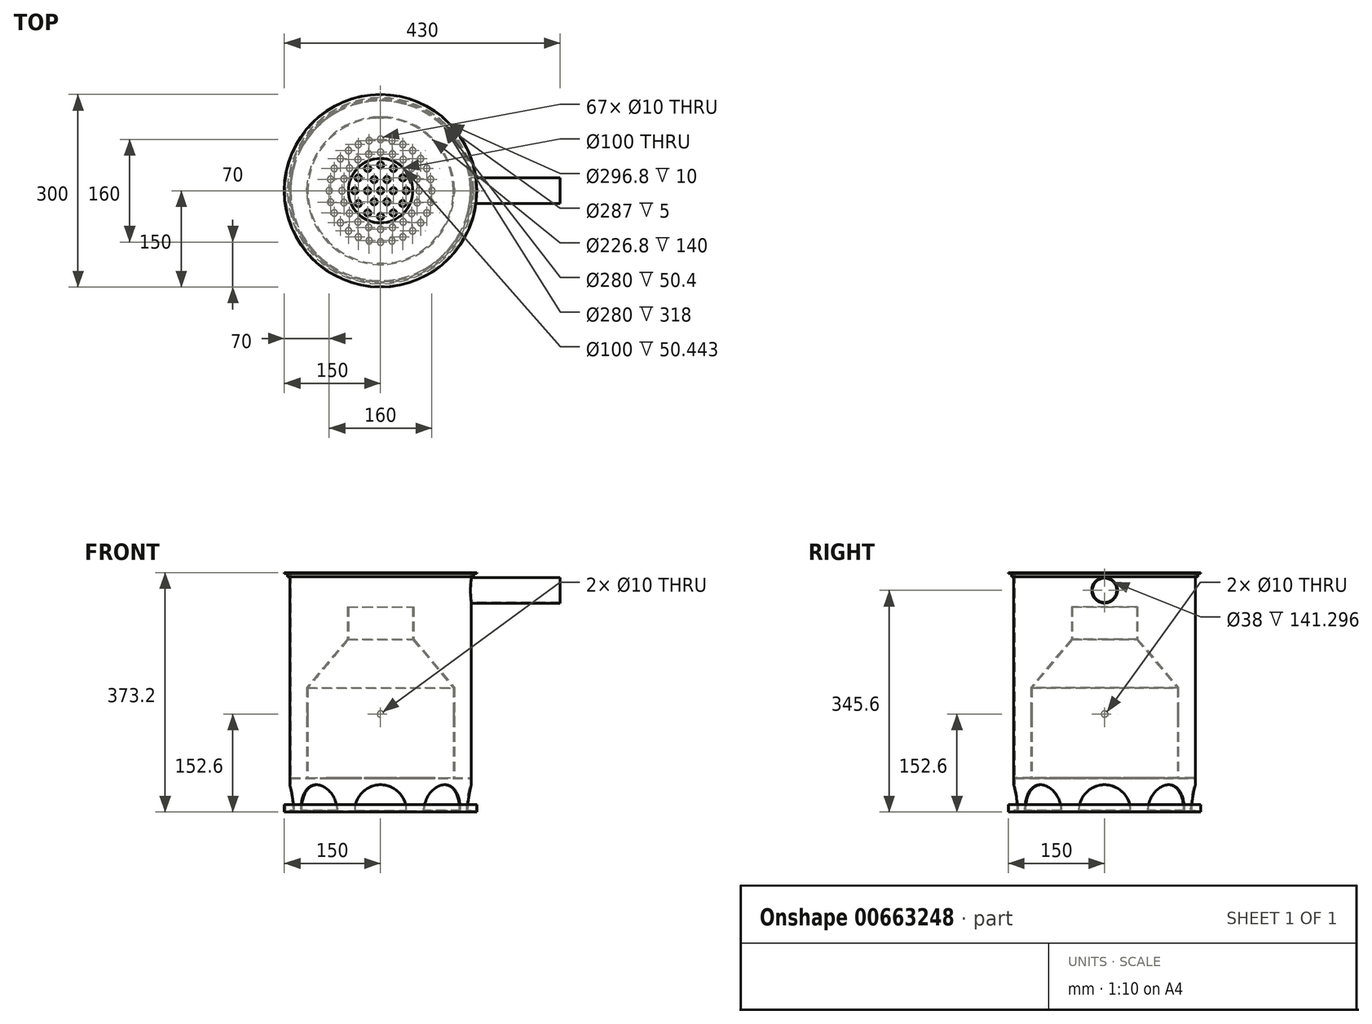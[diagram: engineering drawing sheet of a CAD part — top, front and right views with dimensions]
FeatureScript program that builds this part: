
annotation { "Feature Type Name" : "Feature", "Feature Type Description" : "" }
export const myFeature = defineFeature(function(context is Context, id is Id, definition is map)
    precondition{}
    {
        {
            var Q0;
            Q0=qCreatedBy(makeId("Front.planeOp"),FACE);
            var sketch = newSketch(context, id + "F0", { "sketchPlane" : qUnion([Q0])});
            skLineSegment(sketch, "E0", {"start": v(140, 0) * mm, "end": v(141.6, 0) * mm});
            skLineSegment(sketch, "E1", {"start": v(141.6, 0) * mm, "end": v(141.6, 370) * mm});
            skLineSegment(sketch, "E2.1", {"start": v(140, 0) * mm, "end": v(140, 370) * mm});
            skLineSegment(sketch, "E3", {"start": v(0, 50.4) * mm, "end": v(140, 50.4) * mm});
            skLineSegment(sketch, "E4", {"start": v(0, 50.4) * mm, "end": v(0, 52) * mm});
            skLineSegment(sketch, "E5", {"start": v(0, 52) * mm, "end": v(140, 52) * mm});
            skLineSegment(sketch, "E6", {"start": v(50, 318) * mm, "end": v(51.6, 318) * mm});
            skLineSegment(sketch, "E7", {"start": v(50, 318) * mm, "end": v(50, 267.56) * mm});
            skLineSegment(sketch, "E8", {"start": v(50, 267.56) * mm, "end": v(113.4, 192) * mm});
            skLineSegment(sketch, "E9", {"start": v(113.4, 192) * mm, "end": v(113.4, 52) * mm});
            skLineSegment(sketch, "E10.0", {"start": v(115, 192.58) * mm, "end": v(115, 52) * mm});
            skLineSegment(sketch, "E10.1", {"start": v(51.6, 268.14) * mm, "end": v(115, 192.58) * mm});
            skLineSegment(sketch, "E10.2", {"start": v(51.6, 318) * mm, "end": v(51.6, 268.14) * mm});
            skLineSegment(sketch, "E11", {"start": v(0, 1) * mm, "end": v(0, 370) * mm, "construction": true});
            skPoint(sketch, "E12.end.orphan", {"position": v(50, 369) * mm});
            skPoint(sketch, "E12.start.orphan", {"position": v(50, 370) * mm});
            skLineSegment(sketch, "E13", {"start": v(141.6, 370) * mm, "end": v(140, 370) * mm});
            skPoint(sketch, "E14.start.orphan", {"position": v(50, 319) * mm});
            skPoint(sketch, "E15.end.orphan", {"position": v(0, 0) * mm});
            skSolve(sketch);
        }
        {
            var Q0;
            Q0=makeQuery(id+"F0.imprint","IMPRINT",FACE,{"disambiguationData":[TD([[makeQuery(id+"F0.imprint","IMPRINT",EDGE,{"derivedFrom":sQuery(id+"F0.wireOp",EDGE,"E0")}),1.0]])]});
            var Q1;
            {var subQ3=sQuery(id+"F0.wireOp",EDGE,"E3");Q1=makeQuery(id+"F0.imprint","IMPRINT",FACE,{"disambiguationData":[TD([[makeQuery(id+"F0.imprint","IMPRINT",EDGE,{"derivedFrom":subQ3}),1.0]])]});}
            var Q2;
            {var subQ0=sQuery(id+"F0.wireOp",EDGE,"E7");Q2=makeQuery(id+"F0.imprint","IMPRINT",FACE,{"disambiguationData":[TD([[makeQuery(id+"F0.imprint","IMPRINT",EDGE,{"derivedFrom":subQ0}),1.0]])]});}
            var Q3;
            {var subQ3=sQuery(id+"F0.wireOp",EDGE,"OUD1FrWK-T3TI-8EPN-yAmI-f2VSRblGpb5R");Q3=makeQuery(id+"F0.imprint","IMPRINT",FACE,{"disambiguationData":[TD([[makeQuery(id+"F0.imprint","IMPRINT",EDGE,{"derivedFrom":subQ3}),-1.0]])]});}
            var Q4;
            Q4=sQuery(id+"F0.wireOp",EDGE,"E11");
            revolve(context, id + "F1", {"entities" : qUnion([Q0, Q1, Q2, Q3]), "axis" : qUnion([Q4]), "revolveType" : RevolveType.FULL});
        }
        {
            var Q0;
            {var subQ0=sQuery(id+"F0.wireOp",EDGE,"E5");Q0=makeQuery(id+"F1.opRevolve","SWEPT_FACE",FACE,{"disambiguationData":[OSD([subQ0]),TDD([makeQuery(id+"F0.imprint","IMPRINT",EDGE,{"disambiguationData":[TD([[makeQuery(id+"F0.imprint","INTERSECT",VERTEX,{"derivedFrom":[sQuery(id+"F0.wireOp",EDGE,"E4"),subQ0]}),-1.0]])],"derivedFrom":subQ0})])]});}
            var sketch = newSketch(context, id + "F2", { "sketchPlane" : qUnion([Q0])});
            skCircle(sketch, "E16", {"center": v(0, 0) * mm, "radius": 5 * mm});
            skCircle(sketch, "E17", {"center": v(20, 0) * mm, "radius": 5 * mm});
            skCircle(sketch, "E18.1.0", {"center": v(10, 17.32) * mm, "radius": 5 * mm});
            skCircle(sketch, "E18.2.0", {"center": v(-10, 17.32) * mm, "radius": 5 * mm});
            skCircle(sketch, "E19.1.3.0", {"center": v(-20, 0) * mm, "radius": 5 * mm});
            skCircle(sketch, "E20", {"center": v(40, 0) * mm, "radius": 5 * mm});
            skCircle(sketch, "E21.1.0", {"center": v(34.64, 20) * mm, "radius": 5 * mm});
            skCircle(sketch, "E21.2.0", {"center": v(20, 34.64) * mm, "radius": 5 * mm});
            skCircle(sketch, "E22.1.3.0", {"center": v(0, 40) * mm, "radius": 5 * mm});
            skCircle(sketch, "E22.1.4.0", {"center": v(-20, 34.64) * mm, "radius": 5 * mm});
            skCircle(sketch, "E22.1.5.0", {"center": v(-34.64, 20) * mm, "radius": 5 * mm});
            skCircle(sketch, "E22.1.6.0", {"center": v(-40, 0) * mm, "radius": 5 * mm});
            skCircle(sketch, "E22.1.7.0", {"center": v(-34.64, -20) * mm, "radius": 5 * mm});
            skCircle(sketch, "E23", {"center": v(60, 0) * mm, "radius": 5 * mm});
            skCircle(sketch, "E24", {"center": v(80, 0) * mm, "radius": 5 * mm});
            skCircle(sketch, "E25.1.0", {"center": v(57.06, 18.54) * mm, "radius": 5 * mm});
            skCircle(sketch, "E25.2.0", {"center": v(48.54, 35.27) * mm, "radius": 5 * mm});
            skCircle(sketch, "E26.1.3.0", {"center": v(35.27, 48.54) * mm, "radius": 5 * mm});
            skCircle(sketch, "E26.1.4.0", {"center": v(18.54, 57.06) * mm, "radius": 5 * mm});
            skCircle(sketch, "E26.1.5.0", {"center": v(0, 60) * mm, "radius": 5 * mm});
            skCircle(sketch, "E26.1.6.0", {"center": v(-18.54, 57.06) * mm, "radius": 5 * mm});
            skCircle(sketch, "E26.1.7.0", {"center": v(-35.27, 48.54) * mm, "radius": 5 * mm});
            skCircle(sketch, "E26.1.8.0", {"center": v(-48.54, 35.27) * mm, "radius": 5 * mm});
            skCircle(sketch, "E26.1.9.0", {"center": v(-57.06, 18.54) * mm, "radius": 5 * mm});
            skCircle(sketch, "E26.1.10.0", {"center": v(-60, 0) * mm, "radius": 5 * mm});
            skCircle(sketch, "E26.1.11.0", {"center": v(-57.06, -18.54) * mm, "radius": 5 * mm});
            skCircle(sketch, "E26.1.12.0", {"center": v(-48.54, -35.27) * mm, "radius": 5 * mm});
            skCircle(sketch, "E26.1.13.0", {"center": v(-35.27, -48.54) * mm, "radius": 5 * mm});
            skCircle(sketch, "E26.1.14.0", {"center": v(-18.54, -57.06) * mm, "radius": 5 * mm});
            skCircle(sketch, "E26.1.15.0", {"center": v(0, -60) * mm, "radius": 5 * mm});
            skCircle(sketch, "E26.1.16.0", {"center": v(18.54, -57.06) * mm, "radius": 5 * mm});
            skCircle(sketch, "E26.1.17.0", {"center": v(35.27, -48.54) * mm, "radius": 5 * mm});
            skCircle(sketch, "E26.1.18.0", {"center": v(48.54, -35.27) * mm, "radius": 5 * mm});
            skCircle(sketch, "E26.1.19.0", {"center": v(57.06, -18.54) * mm, "radius": 5 * mm});
            skCircle(sketch, "E27.1.8.0", {"center": v(-20, -34.64) * mm, "radius": 5 * mm});
            skCircle(sketch, "E27.1.9.0", {"center": v(0, -40) * mm, "radius": 5 * mm});
            skCircle(sketch, "E27.1.10.0", {"center": v(20, -34.64) * mm, "radius": 5 * mm});
            skCircle(sketch, "E27.1.11.0", {"center": v(34.64, -20) * mm, "radius": 5 * mm});
            skCircle(sketch, "E28.1.0", {"center": v(78, 17.8) * mm, "radius": 5 * mm});
            skCircle(sketch, "E28.2.0", {"center": v(72.08, 34.71) * mm, "radius": 5 * mm});
            skCircle(sketch, "E29.1.3.0", {"center": v(62.55, 49.88) * mm, "radius": 5 * mm});
            skCircle(sketch, "E29.1.4.0", {"center": v(49.88, 62.55) * mm, "radius": 5 * mm});
            skCircle(sketch, "E29.1.5.0", {"center": v(34.71, 72.08) * mm, "radius": 5 * mm});
            skCircle(sketch, "E29.1.6.0", {"center": v(17.8, 78) * mm, "radius": 5 * mm});
            skCircle(sketch, "E29.1.7.0", {"center": v(0, 80) * mm, "radius": 5 * mm});
            skCircle(sketch, "E29.1.8.0", {"center": v(-17.8, 78) * mm, "radius": 5 * mm});
            skCircle(sketch, "E29.1.9.0", {"center": v(-34.71, 72.08) * mm, "radius": 5 * mm});
            skCircle(sketch, "E29.1.10.0", {"center": v(-49.88, 62.55) * mm, "radius": 5 * mm});
            skCircle(sketch, "E29.1.11.0", {"center": v(-62.55, 49.88) * mm, "radius": 5 * mm});
            skCircle(sketch, "E29.1.12.0", {"center": v(-72.08, 34.71) * mm, "radius": 5 * mm});
            skCircle(sketch, "E29.1.13.0", {"center": v(-78, 17.8) * mm, "radius": 5 * mm});
            skCircle(sketch, "E29.1.14.0", {"center": v(-80, 0) * mm, "radius": 5 * mm});
            skCircle(sketch, "E29.1.15.0", {"center": v(-78, -17.8) * mm, "radius": 5 * mm});
            skCircle(sketch, "E29.1.16.0", {"center": v(-72.08, -34.71) * mm, "radius": 5 * mm});
            skCircle(sketch, "E29.1.17.0", {"center": v(-62.55, -49.88) * mm, "radius": 5 * mm});
            skCircle(sketch, "E29.1.18.0", {"center": v(-49.88, -62.55) * mm, "radius": 5 * mm});
            skCircle(sketch, "E29.1.19.0", {"center": v(-34.71, -72.08) * mm, "radius": 5 * mm});
            skCircle(sketch, "E29.1.20.0", {"center": v(-17.8, -78) * mm, "radius": 5 * mm});
            skCircle(sketch, "E29.1.21.0", {"center": v(0, -80) * mm, "radius": 5 * mm});
            skCircle(sketch, "E29.1.22.0", {"center": v(17.8, -78) * mm, "radius": 5 * mm});
            skCircle(sketch, "E29.1.23.0", {"center": v(34.71, -72.08) * mm, "radius": 5 * mm});
            skCircle(sketch, "E29.1.24.0", {"center": v(49.88, -62.55) * mm, "radius": 5 * mm});
            skCircle(sketch, "E29.1.25.0", {"center": v(62.55, -49.88) * mm, "radius": 5 * mm});
            skCircle(sketch, "E29.1.26.0", {"center": v(72.08, -34.71) * mm, "radius": 5 * mm});
            skCircle(sketch, "E29.1.27.0", {"center": v(78, -17.8) * mm, "radius": 5 * mm});
            skCircle(sketch, "E30.1.4.0", {"center": v(-10, -17.32) * mm, "radius": 5 * mm});
            skCircle(sketch, "E30.1.5.0", {"center": v(10, -17.32) * mm, "radius": 5 * mm});
            skSolve(sketch);
        }
        {
            var Q0;
            Q0=qSketchRegion(id+"F2",true);
            var Q1;
            Q1=makeQuery(id+"F1.opRevolve","SWEPT_FACE",FACE,{"disambiguationData":[OSD([sQuery(id+"F0.wireOp",EDGE,"E3")])]});
            extrude(context, id + "F3", {"entities" : qUnion([Q0]), "operationType" : NewBodyOperationType.REMOVE, "endBound" : BoundingType.UP_TO_SURFACE, "oppositeDirection" : true, "depth" : 1 * mm, "endBoundEntityFace" : qUnion([Q1]), "offsetDistance" : 25 * mm});
        }
        {
            var Q0;
            Q0=qCreatedBy(makeId("Right.planeOp"),FACE);
            var sketch = newSketch(context, id + "F4", { "sketchPlane" : qUnion([Q0])});
            skCircle(sketch, "E31", {"center": v(0, 344) * mm, "radius": 20 * mm});
            skSolve(sketch);
        }
        {
            var Q0;
            Q0=makeQuery(id+"F4.imprint","IMPRINT",FACE,{"disambiguationData":[TD([[makeQuery(id+"F4.imprint","IMPRINT",EDGE,{"derivedFrom":sQuery(id+"F4.wireOp",EDGE,"E31")}),1.0]])]});
            var Q1;
            Q1=sQuery(id+"F4.wireOp",EDGE,"E31");
            extrude(context, id + "F5", {"entities" : qUnion([Q0]), "operationType" : NewBodyOperationType.ADD, "surfaceEntities" : qUnion([Q1]), "depth" : 280 * mm, "offsetDistance" : 25 * mm});
        }
        {
            var Q0;
            Q0=makeQuery(id+"F5.opExtrude","CAP_FACE",FACE,{"disambiguationData":[OSD([sQuery(id+"F4.wireOp",EDGE,"E31")])],"isStart":true});
            var sketch = newSketch(context, id + "F6", { "sketchPlane" : qUnion([Q0])});
            skCircle(sketch, "E32", {"center": v(0, 344) * mm, "radius": 19 * mm});
            skSolve(sketch);
        }
        {
            var Q0;
            Q0=makeQuery(id+"F6.imprint","IMPRINT",FACE,{"disambiguationData":[TD([[makeQuery(id+"F6.imprint","IMPRINT",EDGE,{"derivedFrom":sQuery(id+"F6.wireOp",EDGE,"E32")}),1.0]])]});
            extrude(context, id + "F7", {"entities" : qUnion([Q0]), "operationType" : NewBodyOperationType.REMOVE, "endBound" : BoundingType.THROUGH_ALL, "oppositeDirection" : true, "depth" : 25 * mm, "offsetDistance" : 25 * mm});
        }
        {
            var Q0;
            Q0=qCreatedBy(makeId("Front.planeOp"),FACE);
            var sketch = newSketch(context, id + "F8", { "sketchPlane" : qUnion([Q0])});
            skLineSegment(sketch, "E33", {"start": v(0, 1) * mm, "end": v(40, 1) * mm});
            skArc(sketch, "E34", {"start": v(40, 1) * mm, "mid": v(0, 41) * mm, "end": v(-40, 1) * mm});
            skLineSegment(sketch, "E35", {"start": v(0, 1) * mm, "end": v(-40, 1) * mm});
            skSolve(sketch);
        }
        {
            var Q0;
            Q0 = qSketchRegion(id + "F8", true);
            extrude(context, id + "F9", {"entities" : qUnion([Q0]), "depth" : 150 * mm, "offsetDistance" : 25 * mm});
        }
        {
            var Q0;
            Q0=makeQuery(id+"F9.opExtrude","SWEPT_BODY",BODY,{"disambiguationData":[OSD([sQuery(id+"F8.wireOp",EDGE,"E33"),sQuery(id+"F8.wireOp",EDGE,"E34"),sQuery(id+"F8.wireOp",EDGE,"E35")])]});
            var Q1;
            Q1=sQuery(id+"F0.wireOp",EDGE,"E11");
            circularPattern(context, id + "F10", {"entities" : qUnion([Q0]), "axis" : qUnion([Q1]), "angle" : 360 * degree, "instanceCount" : 8, "equalSpace" : true});
        }
        {
            var Q0;
            Q0=makeQuery(id+"F9.opExtrude","SWEPT_BODY",BODY,{"disambiguationData":[OSD([sQuery(id+"F8.wireOp",EDGE,"E33"),sQuery(id+"F8.wireOp",EDGE,"E34"),sQuery(id+"F8.wireOp",EDGE,"E35")])]});
            var Q1;
            Q1=makeQuery(id+"F10.opPattern","COPY",BODY,{"derivedFrom":makeQuery(id+"F9.opExtrude","SWEPT_BODY",BODY,{"disambiguationData":[OSD([sQuery(id+"F8.wireOp",EDGE,"E33"),sQuery(id+"F8.wireOp",EDGE,"E34"),sQuery(id+"F8.wireOp",EDGE,"E35")])]}),"instanceName":"1"});
            var Q2;
            Q2=makeQuery(id+"F10.opPattern","COPY",BODY,{"derivedFrom":makeQuery(id+"F9.opExtrude","SWEPT_BODY",BODY,{"disambiguationData":[OSD([sQuery(id+"F8.wireOp",EDGE,"E33"),sQuery(id+"F8.wireOp",EDGE,"E34"),sQuery(id+"F8.wireOp",EDGE,"E35")])]}),"instanceName":"2"});
            var Q3;
            Q3=makeQuery(id+"F10.opPattern","COPY",BODY,{"derivedFrom":makeQuery(id+"F9.opExtrude","SWEPT_BODY",BODY,{"disambiguationData":[OSD([sQuery(id+"F8.wireOp",EDGE,"E33"),sQuery(id+"F8.wireOp",EDGE,"E34"),sQuery(id+"F8.wireOp",EDGE,"E35")])]}),"instanceName":"3"});
            var Q4;
            Q4=makeQuery(id+"F10.opPattern","COPY",BODY,{"derivedFrom":makeQuery(id+"F9.opExtrude","SWEPT_BODY",BODY,{"disambiguationData":[OSD([sQuery(id+"F8.wireOp",EDGE,"E33"),sQuery(id+"F8.wireOp",EDGE,"E34"),sQuery(id+"F8.wireOp",EDGE,"E35")])]}),"instanceName":"4"});
            var Q5;
            Q5=makeQuery(id+"F10.opPattern","COPY",BODY,{"derivedFrom":makeQuery(id+"F9.opExtrude","SWEPT_BODY",BODY,{"disambiguationData":[OSD([sQuery(id+"F8.wireOp",EDGE,"E33"),sQuery(id+"F8.wireOp",EDGE,"E34"),sQuery(id+"F8.wireOp",EDGE,"E35")])]}),"instanceName":"5"});
            var Q6;
            Q6=makeQuery(id+"F10.opPattern","COPY",BODY,{"derivedFrom":makeQuery(id+"F9.opExtrude","SWEPT_BODY",BODY,{"disambiguationData":[OSD([sQuery(id+"F8.wireOp",EDGE,"E33"),sQuery(id+"F8.wireOp",EDGE,"E34"),sQuery(id+"F8.wireOp",EDGE,"E35")])]}),"instanceName":"6"});
            var Q7;
            Q7=makeQuery(id+"F10.opPattern","COPY",BODY,{"derivedFrom":makeQuery(id+"F9.opExtrude","SWEPT_BODY",BODY,{"disambiguationData":[OSD([sQuery(id+"F8.wireOp",EDGE,"E33"),sQuery(id+"F8.wireOp",EDGE,"E34"),sQuery(id+"F8.wireOp",EDGE,"E35")])]}),"instanceName":"7"});
            var Q8;
            Q8=makeQuery(id+"F1.opRevolve","SWEPT_BODY",BODY,{"disambiguationData":[OSD([sQuery(id+"F0.wireOp",EDGE,"E0"),sQuery(id+"F0.wireOp",EDGE,"E1"),sQuery(id+"F0.wireOp",EDGE,"noxKHUUk-OG0o-8wTU-6CPF-3SisgwZ0xtMZ"),sQuery(id+"F0.wireOp",EDGE,"E2.0"),sQuery(id+"F0.wireOp",EDGE,"E2.1"),sQuery(id+"F0.wireOp",EDGE,"E2.2"),sQuery(id+"F0.wireOp",EDGE,"E12"),sQuery(id+"F0.wireOp",EDGE,"E15"),sQuery(id+"F0.wireOp",EDGE,"E3"),sQuery(id+"F0.wireOp",EDGE,"E4"),sQuery(id+"F0.wireOp",EDGE,"E5"),sQuery(id+"F0.wireOp",EDGE,"OUD1FrWK-T3TI-8EPN-yAmI-f2VSRblGpb5R"),sQuery(id+"F0.wireOp",EDGE,"E14"),sQuery(id+"F0.wireOp",EDGE,"E6"),sQuery(id+"F0.wireOp",EDGE,"E7"),sQuery(id+"F0.wireOp",EDGE,"E8"),sQuery(id+"F0.wireOp",EDGE,"E9"),sQuery(id+"F0.wireOp",EDGE,"E10.0"),sQuery(id+"F0.wireOp",EDGE,"E10.1"),sQuery(id+"F0.wireOp",EDGE,"E10.2")])]});
            booleanBodies(context, id + "F11", {"operationType" : BooleanOperationType.SUBTRACTION, "tools" : qUnion([Q0, Q1, Q2, Q3, Q4, Q5, Q6, Q7]), "targets" : qUnion([Q8])});
        }
        {
            var Q0;
            Q0=qCreatedBy(makeId("Front.planeOp"),FACE);
            var sketch = newSketch(context, id + "F12", { "sketchPlane" : qUnion([Q0])});
            skCircle(sketch, "E36", {"center": v(0, 151) * mm, "radius": 5 * mm});
            skSolve(sketch);
        }
        {
            var Q0;
            Q0 = qSketchRegion(id + "F12", true);
            extrude(context, id + "F13", {"entities" : qUnion([Q0]), "depth" : 128 * mm, "offsetDistance" : 25 * mm});
        }
        {
            var Q0;
            Q0=makeQuery(id+"F13.opExtrude","SWEPT_BODY",BODY,{"disambiguationData":[OSD([sQuery(id+"F12.wireOp",EDGE,"E36")])]});
            var Q1;
            Q1=sQuery(id+"F0.wireOp",EDGE,"E11");
            circularPattern(context, id + "F14", {"entities" : qUnion([Q0]), "axis" : qUnion([Q1]), "angle" : 360 * degree, "instanceCount" : 4, "equalSpace" : true});
        }
        {
            var Q0;
            Q0=makeQuery(id+"F14.opPattern","COPY",BODY,{"derivedFrom":makeQuery(id+"F13.opExtrude","SWEPT_BODY",BODY,{"disambiguationData":[OSD([sQuery(id+"F12.wireOp",EDGE,"E36")])]}),"instanceName":"2"});
            var Q1;
            Q1=makeQuery(id+"F14.opPattern","COPY",BODY,{"derivedFrom":makeQuery(id+"F13.opExtrude","SWEPT_BODY",BODY,{"disambiguationData":[OSD([sQuery(id+"F12.wireOp",EDGE,"E36")])]}),"instanceName":"3"});
            var Q2;
            Q2=makeQuery(id+"F14.opPattern","COPY",BODY,{"derivedFrom":makeQuery(id+"F13.opExtrude","SWEPT_BODY",BODY,{"disambiguationData":[OSD([sQuery(id+"F12.wireOp",EDGE,"E36")])]}),"instanceName":"1"});
            var Q3;
            Q3=makeQuery(id+"F13.opExtrude","SWEPT_BODY",BODY,{"disambiguationData":[OSD([sQuery(id+"F12.wireOp",EDGE,"E36")])]});
            var Q4;
            Q4=makeQuery(id+"F1.opRevolve","SWEPT_BODY",BODY,{"disambiguationData":[OSD([sQuery(id+"F0.wireOp",EDGE,"E0"),sQuery(id+"F0.wireOp",EDGE,"E1"),sQuery(id+"F0.wireOp",EDGE,"noxKHUUk-OG0o-8wTU-6CPF-3SisgwZ0xtMZ"),sQuery(id+"F0.wireOp",EDGE,"E2.0"),sQuery(id+"F0.wireOp",EDGE,"E2.1"),sQuery(id+"F0.wireOp",EDGE,"E2.2"),sQuery(id+"F0.wireOp",EDGE,"E12"),sQuery(id+"F0.wireOp",EDGE,"E15"),sQuery(id+"F0.wireOp",EDGE,"E3"),sQuery(id+"F0.wireOp",EDGE,"E4"),sQuery(id+"F0.wireOp",EDGE,"E5"),sQuery(id+"F0.wireOp",EDGE,"OUD1FrWK-T3TI-8EPN-yAmI-f2VSRblGpb5R"),sQuery(id+"F0.wireOp",EDGE,"E14"),sQuery(id+"F0.wireOp",EDGE,"E6"),sQuery(id+"F0.wireOp",EDGE,"E7"),sQuery(id+"F0.wireOp",EDGE,"E8"),sQuery(id+"F0.wireOp",EDGE,"E9"),sQuery(id+"F0.wireOp",EDGE,"E10.0"),sQuery(id+"F0.wireOp",EDGE,"E10.1"),sQuery(id+"F0.wireOp",EDGE,"E10.2")])]});
            booleanBodies(context, id + "F15", {"operationType" : BooleanOperationType.SUBTRACTION, "tools" : qUnion([Q0, Q1, Q2, Q3]), "targets" : qUnion([Q4])});
        }
        {
            var Q0;
            Q0=makeQuery(id+"F1.opRevolve","SWEPT_FACE",FACE,{"disambiguationData":[OSD([sQuery(id+"F0.wireOp",EDGE,"E13")])]});
            var sketch = newSketch(context, id + "F16", { "sketchPlane" : qUnion([Q0])});
            skCircle(sketch, "E37", {"center": v(0, 0) * mm, "radius": 140 * mm});
            skSolve(sketch);
        }
        {
            var Q0;
            Q0 = qSketchRegion(id + "F16", true);
            var Q1;
            Q1=makeQuery(id+"F1.opRevolve","SWEPT_FACE",FACE,{"disambiguationData":[OSD([sQuery(id+"F0.wireOp",EDGE,"E6")])]});
            extrude(context, id + "F17", {"entities" : qUnion([Q0]), "operationType" : NewBodyOperationType.REMOVE, "endBound" : BoundingType.UP_TO_SURFACE, "oppositeDirection" : true, "depth" : 25 * mm, "endBoundEntityFace" : qUnion([Q1]), "offsetDistance" : 25 * mm});
        }
        {
            var Q0;
            Q0=makeQuery(id+"F1.opRevolve","SWEPT_FACE",FACE,{"disambiguationData":[OSD([sQuery(id+"F0.wireOp",EDGE,"E13")])]});
            var sketch = newSketch(context, id + "F18", { "sketchPlane" : qUnion([Q0])});
            skCircle(sketch, "E38", {"center": v(0, 0) * mm, "radius": 150 * mm});
            skSolve(sketch);
        }
        {
            var Q0;
            Q0 = qSketchRegion(id + "F18", true);
            extrude(context, id + "F19", {"entities" : qUnion([Q0]), "depth" : 1.6 * mm, "offsetDistance" : 25 * mm});
        }
        {
            var Q0;
            Q0=makeQuery(id+"F19.opExtrude","CAP_FACE",FACE,{"disambiguationData":[OSD([sQuery(id+"F18.wireOp",EDGE,"E38")])],"isStart":true});
            var sketch = newSketch(context, id + "F20", { "sketchPlane" : qUnion([Q0])});
            skCircle(sketch, "E39", {"center": v(0, 0) * mm, "radius": 143.5 * mm});
            skCircle(sketch, "E40.0", {"center": v(0, 0) * mm, "radius": 145.1 * mm});
            skSolve(sketch);
        }
        {
            var Q0;
            Q0=makeQuery(id+"F19.opExtrude","CAP_FACE",FACE,{"disambiguationData":[OSD([sQuery(id+"F18.wireOp",EDGE,"E38")])],"isStart":false});
            var sketch = newSketch(context, id + "F21", { "sketchPlane" : qUnion([Q0])});
            skCircle(sketch, "E41", {"center": v(0, 0) * mm, "radius": 50 * mm});
            skSolve(sketch);
        }
        {
            var Q0;
            Q0 = qSketchRegion(id + "F21", true);
            extrude(context, id + "F22", {"entities" : qUnion([Q0]), "operationType" : NewBodyOperationType.REMOVE, "oppositeDirection" : true, "depth" : 2 * mm, "offsetDistance" : 25 * mm});
        }
        {
            var Q0;
            Q0=makeQuery(id+"F1.opRevolve","SWEPT_FACE",FACE,{"disambiguationData":[OSD([sQuery(id+"F0.wireOp",EDGE,"E0")])]});
            var sketch = newSketch(context, id + "F23", { "sketchPlane" : qUnion([Q0])});
            skCircle(sketch, "E42", {"center": v(0, 0) * mm, "radius": 150 * mm});
            skSolve(sketch);
        }
        {
            var Q0;
            Q0 = qSketchRegion(id + "F23", true);
            extrude(context, id + "F24", {"entities" : qUnion([Q0]), "depth" : 1.6 * mm, "offsetDistance" : 25 * mm});
        }
        {
            var Q0;
            Q0=makeQuery(id+"F24.opExtrude","CAP_FACE",FACE,{"disambiguationData":[OSD([sQuery(id+"F23.wireOp",EDGE,"E42")])],"isStart":true});
            var sketch = newSketch(context, id + "F25", { "sketchPlane" : qUnion([Q0])});
            skCircle(sketch, "E43", {"center": v(0, 0) * mm, "radius": 148.4 * mm});
            skSolve(sketch);
        }
        {
            var Q0;
            Q0=makeQuery(id+"F25.imprint","IMPRINT",FACE,{"disambiguationData":[TD([[makeQuery(id+"F25.imprint","IMPRINT",EDGE,{"derivedFrom":sQuery(id+"F25.wireOp",EDGE,"E43")}),-1.0]])]});
            extrude(context, id + "F26", {"entities" : qUnion([Q0]), "operationType" : NewBodyOperationType.ADD, "depth" : 10 * mm, "offsetDistance" : 25 * mm});
        }
        {
            var Q0;
            Q0=makeQuery(id+"F20.imprint","IMPRINT",FACE,{"disambiguationData":[TD([[makeQuery(id+"F20.imprint","IMPRINT",EDGE,{"derivedFrom":sQuery(id+"F20.wireOp",EDGE,"E39")}),-1.0]])]});
            extrude(context, id + "F27", {"entities" : qUnion([Q0]), "depth" : 5 * mm, "offsetDistance" : 25 * mm});
        }
    });
